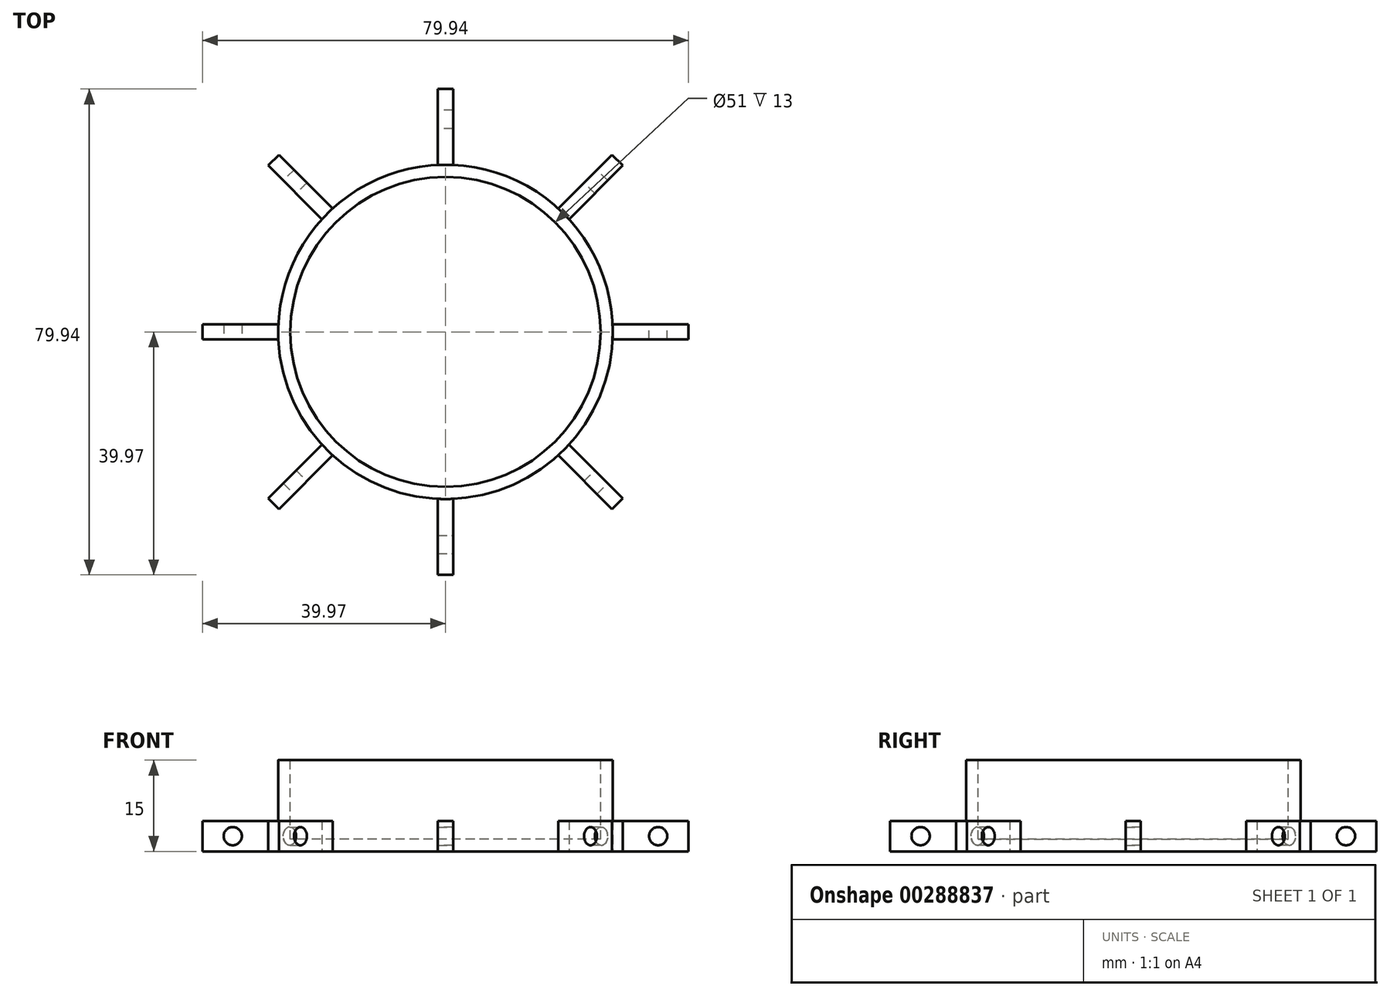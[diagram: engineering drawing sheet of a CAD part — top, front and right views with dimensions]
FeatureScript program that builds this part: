
annotation { "Feature Type Name" : "Feature", "Feature Type Description" : "" }
export const myFeature = defineFeature(function(context is Context, id is Id, definition is map)
    precondition{}
    {
        {
            var Q0;
            Q0=qCreatedBy(makeId("Top.planeOp"),FACE);
            var sketch = newSketch(context, id + "F0", { "sketchPlane" : qUnion([Q0])});
            skCircle(sketch, "E0", {"center": v(0, 0) * mm, "radius": 27.5 * mm});
            skPoint(sketch, "E1", {"position": v(0, 27.5) * mm});
            skLineSegment(sketch, "E2.bottom", {"start": v(1.25, 39.97) * mm, "end": v(-1.25, 39.97) * mm});
            skLineSegment(sketch, "E2.left", {"start": v(1.25, 39.97) * mm, "end": v(1.25, 27.47) * mm});
            skLineSegment(sketch, "E2.right", {"start": v(-1.25, 39.97) * mm, "end": v(-1.25, 27.47) * mm});
            skLineSegment(sketch, "E3.MirrorCS", {"start": v(-1.25, -39.97) * mm, "end": v(-1.25, -27.47) * mm});
            skLineSegment(sketch, "E4.MirrorCS", {"start": v(1.25, -39.97) * mm, "end": v(1.25, -27.47) * mm});
            skLineSegment(sketch, "E5.MirrorCS", {"start": v(1.25, -39.97) * mm, "end": v(-1.25, -39.97) * mm});
            skPoint(sketch, "E6", {"position": v(-27.5, 0) * mm});
            skLineSegment(sketch, "E7.MirrorCS", {"start": v(-39.97, 1.25) * mm, "end": v(-27.47, 1.25) * mm});
            skLineSegment(sketch, "E8.MirrorCS", {"start": v(-39.97, -1.25) * mm, "end": v(-27.47, -1.25) * mm});
            skLineSegment(sketch, "E9.MirrorCS", {"start": v(-39.97, -1.25) * mm, "end": v(-39.97, 1.25) * mm});
            skLineSegment(sketch, "E10.MirrorCS", {"start": v(-27.38, 29.15) * mm, "end": v(-18.54, 20.3) * mm});
            skLineSegment(sketch, "E11.MirrorCS", {"start": v(-29.15, 27.38) * mm, "end": v(-20.3, 18.54) * mm});
            skLineSegment(sketch, "E12.MirrorCS", {"start": v(-29.15, 27.38) * mm, "end": v(-27.38, 29.15) * mm});
            skLineSegment(sketch, "E13.MirrorCS", {"start": v(-27.38, -29.15) * mm, "end": v(-18.54, -20.3) * mm});
            skLineSegment(sketch, "E14.MirrorCS", {"start": v(-29.15, -27.38) * mm, "end": v(-20.3, -18.54) * mm});
            skLineSegment(sketch, "E15.MirrorCS", {"start": v(-29.15, -27.38) * mm, "end": v(-27.38, -29.15) * mm});
            skLineSegment(sketch, "E16.MirrorCS", {"start": v(39.97, 1.25) * mm, "end": v(27.47, 1.25) * mm});
            skLineSegment(sketch, "E17.MirrorCS", {"start": v(39.97, -1.25) * mm, "end": v(27.47, -1.25) * mm});
            skLineSegment(sketch, "E18.MirrorCS", {"start": v(39.97, -1.25) * mm, "end": v(39.97, 1.25) * mm});
            skLineSegment(sketch, "E19.MirrorCS", {"start": v(27.38, -29.15) * mm, "end": v(18.54, -20.3) * mm});
            skLineSegment(sketch, "E20.MirrorCS", {"start": v(29.15, -27.38) * mm, "end": v(20.3, -18.54) * mm});
            skLineSegment(sketch, "E21.MirrorCS", {"start": v(29.15, -27.38) * mm, "end": v(27.38, -29.15) * mm});
            skLineSegment(sketch, "E22.MirrorCS", {"start": v(29.15, 27.38) * mm, "end": v(20.3, 18.54) * mm});
            skLineSegment(sketch, "E23.MirrorCS", {"start": v(27.38, 29.15) * mm, "end": v(18.54, 20.3) * mm});
            skLineSegment(sketch, "E24.MirrorCS", {"start": v(29.15, 27.38) * mm, "end": v(27.38, 29.15) * mm});
            skSolve(sketch);
        }
        {
            var Q0;
            Q0=makeQuery(id+"F0.imprint","IMPRINT",FACE,{"disambiguationData":[TD([[makeQuery(id+"F0.imprint","IMPRINT",EDGE,{"derivedFrom":sQuery(id+"F0.wireOp",EDGE,"E0")}),1.0]])]});
            extrude(context, id + "F1", {"entities" : qUnion([Q0]), "depth" : 15 * mm});
        }
        {
            var Q0;
            Q0=makeQuery(id+"F1.opExtrude","CAP_FACE",FACE,{"disambiguationData":[OSD([sQuery(id+"F0.wireOp",EDGE,"E0")])],"isStart":false});
            var sketch = newSketch(context, id + "F2", { "sketchPlane" : qUnion([Q0])});
            skCircle(sketch, "E25", {"center": v(0, 0) * mm, "radius": 25.5 * mm});
            skSolve(sketch);
        }
        {
            var Q0;
            Q0=makeQuery(id+"F2.imprint","IMPRINT",FACE,{"disambiguationData":[TD([[makeQuery(id+"F2.imprint","IMPRINT",EDGE,{"derivedFrom":sQuery(id+"F2.wireOp",EDGE,"E25")}),1.0]])]});
            extrude(context, id + "F3", {"entities" : qUnion([Q0]), "operationType" : NewBodyOperationType.REMOVE, "oppositeDirection" : true, "depth" : 13 * mm});
        }
        {
            var Q0;
            Q0=makeQuery(id+"F0.imprint","IMPRINT",FACE,{"disambiguationData":[TD([[makeQuery(id+"F0.imprint","IMPRINT",EDGE,{"derivedFrom":sQuery(id+"F0.wireOp",EDGE,"E2.bottom")}),1.0]])]});
            var Q1;
            {var subQ0=sQuery(id+"F0.wireOp",EDGE,"E10.MirrorCS");Q1=makeQuery(id+"F0.imprint","IMPRINT",FACE,{"disambiguationData":[TD([[makeQuery(id+"F0.imprint","IMPRINT",EDGE,{"derivedFrom":subQ0}),-1.0]])]});}
            var Q2;
            {var subQ0=sQuery(id+"F0.wireOp",EDGE,"E7.MirrorCS");Q2=makeQuery(id+"F0.imprint","IMPRINT",FACE,{"disambiguationData":[TD([[makeQuery(id+"F0.imprint","IMPRINT",EDGE,{"derivedFrom":subQ0}),-1.0]])]});}
            var Q3;
            {var subQ0=sQuery(id+"F0.wireOp",EDGE,"E13.MirrorCS");Q3=makeQuery(id+"F0.imprint","IMPRINT",FACE,{"disambiguationData":[TD([[makeQuery(id+"F0.imprint","IMPRINT",EDGE,{"derivedFrom":subQ0}),1.0]])]});}
            var Q4;
            {var subQ0=sQuery(id+"F0.wireOp",EDGE,"E3.MirrorCS");Q4=makeQuery(id+"F0.imprint","IMPRINT",FACE,{"disambiguationData":[TD([[makeQuery(id+"F0.imprint","IMPRINT",EDGE,{"derivedFrom":subQ0}),-1.0]])]});}
            var Q5;
            {var subQ0=sQuery(id+"F0.wireOp",EDGE,"E19.MirrorCS");Q5=makeQuery(id+"F0.imprint","IMPRINT",FACE,{"disambiguationData":[TD([[makeQuery(id+"F0.imprint","IMPRINT",EDGE,{"derivedFrom":subQ0}),-1.0]])]});}
            var Q6;
            {var subQ0=sQuery(id+"F0.wireOp",EDGE,"E16.MirrorCS");Q6=makeQuery(id+"F0.imprint","IMPRINT",FACE,{"disambiguationData":[TD([[makeQuery(id+"F0.imprint","IMPRINT",EDGE,{"derivedFrom":subQ0}),1.0]])]});}
            var Q7;
            {var subQ0=sQuery(id+"F0.wireOp",EDGE,"E22.MirrorCS");Q7=makeQuery(id+"F0.imprint","IMPRINT",FACE,{"disambiguationData":[TD([[makeQuery(id+"F0.imprint","IMPRINT",EDGE,{"derivedFrom":subQ0}),-1.0]])]});}
            extrude(context, id + "F4", {"entities" : qUnion([Q0, Q1, Q2, Q3, Q4, Q5, Q6, Q7]), "operationType" : NewBodyOperationType.ADD, "depth" : 5 * mm});
        }
        {
            var Q0;
            Q0=makeQuery(id+"F4.opExtrude","SWEPT_FACE",FACE,{"disambiguationData":[OSD([sQuery(id+"F0.wireOp",EDGE,"E4.MirrorCS")])]});
            var sketch = newSketch(context, id + "F5", { "sketchPlane" : qUnion([Q0])});
            skLineSegment(sketch, "E26", {"start": v(-39.97, 2.5) * mm, "end": v(-34.97, 2.5) * mm});
            skCircle(sketch, "E27", {"center": v(-34.97, 2.5) * mm, "radius": 1.5 * mm});
            skSolve(sketch);
        }
        {
            var Q0;
            Q0=makeQuery(id+"F5.imprint","IMPRINT",FACE,{"disambiguationData":[TD([[makeQuery(id+"F5.imprint","IMPRINT",EDGE,{"derivedFrom":sQuery(id+"F5.wireOp",EDGE,"E27")}),1.0]])]});
            extrude(context, id + "F6", {"entities" : qUnion([Q0]), "operationType" : NewBodyOperationType.REMOVE, "oppositeDirection" : true, "depth" : 25 * mm});
        }
        {
            var Q0;
            Q0=makeQuery(id+"F4.opExtrude","SWEPT_FACE",FACE,{"disambiguationData":[OSD([sQuery(id+"F0.wireOp",EDGE,"E13.MirrorCS")])]});
            var sketch = newSketch(context, id + "F7", { "sketchPlane" : qUnion([Q0])});
            skLineSegment(sketch, "E28", {"start": v(-39.97, 2.5) * mm, "end": v(-34.97, 2.5) * mm});
            skCircle(sketch, "E29", {"center": v(-34.97, 2.5) * mm, "radius": 1.5 * mm});
            skSolve(sketch);
        }
        {
            var Q0;
            Q0=makeQuery(id+"F7.imprint","IMPRINT",FACE,{"disambiguationData":[TD([[makeQuery(id+"F7.imprint","IMPRINT",EDGE,{"derivedFrom":sQuery(id+"F7.wireOp",EDGE,"E29")}),1.0]])]});
            var Q1;
            Q1=sQuery(id+"F7.wireOp",EDGE,"E29");
            extrude(context, id + "F8", {"entities" : qUnion([Q0]), "operationType" : NewBodyOperationType.REMOVE, "surfaceEntities" : qUnion([Q1]), "oppositeDirection" : true, "depth" : 25 * mm});
        }
        {
            var Q0;
            Q0=makeQuery(id+"F4.opExtrude","SWEPT_FACE",FACE,{"disambiguationData":[OSD([sQuery(id+"F0.wireOp",EDGE,"E8.MirrorCS")])]});
            var sketch = newSketch(context, id + "F9", { "sketchPlane" : qUnion([Q0])});
            skLineSegment(sketch, "E30", {"start": v(-39.97, 2.5) * mm, "end": v(-34.97, 2.5) * mm});
            skPoint(sketch, "E30.endSnap0", {"position": v(-39.97, 2.5) * mm});
            skCircle(sketch, "E31", {"center": v(-34.97, 2.5) * mm, "radius": 1.5 * mm});
            skSolve(sketch);
        }
        {
            var Q0;
            Q0=makeQuery(id+"F9.imprint","IMPRINT",FACE,{"disambiguationData":[TD([[makeQuery(id+"F9.imprint","IMPRINT",EDGE,{"derivedFrom":sQuery(id+"F9.wireOp",EDGE,"E31")}),1.0]])]});
            extrude(context, id + "F10", {"entities" : qUnion([Q0]), "operationType" : NewBodyOperationType.REMOVE, "oppositeDirection" : true, "depth" : 25 * mm});
        }
        {
            var Q0;
            Q0=makeQuery(id+"F4.opExtrude","SWEPT_FACE",FACE,{"disambiguationData":[OSD([sQuery(id+"F0.wireOp",EDGE,"E11.MirrorCS")])]});
            var sketch = newSketch(context, id + "F11", { "sketchPlane" : qUnion([Q0])});
            skLineSegment(sketch, "E32", {"start": v(-39.97, 2.5) * mm, "end": v(-34.97, 2.5) * mm});
            skCircle(sketch, "E33", {"center": v(-34.97, 2.5) * mm, "radius": 1.5 * mm});
            skSolve(sketch);
        }
        {
            var Q0;
            Q0=makeQuery(id+"F11.imprint","IMPRINT",FACE,{"disambiguationData":[TD([[makeQuery(id+"F11.imprint","IMPRINT",EDGE,{"derivedFrom":sQuery(id+"F11.wireOp",EDGE,"E33")}),1.0]])]});
            extrude(context, id + "F12", {"entities" : qUnion([Q0]), "operationType" : NewBodyOperationType.REMOVE, "oppositeDirection" : true, "depth" : 25 * mm});
        }
        {
            var Q0;
            Q0=makeQuery(id+"F4.opExtrude","SWEPT_FACE",FACE,{"disambiguationData":[OSD([sQuery(id+"F0.wireOp",EDGE,"E2.right")])]});
            var sketch = newSketch(context, id + "F13", { "sketchPlane" : qUnion([Q0])});
            skLineSegment(sketch, "E34", {"start": v(-39.97, 2.5) * mm, "end": v(-34.97, 2.5) * mm});
            skCircle(sketch, "E35", {"center": v(-34.97, 2.5) * mm, "radius": 1.5 * mm});
            skSolve(sketch);
        }
        {
            var Q0;
            Q0=makeQuery(id+"F13.imprint","IMPRINT",FACE,{"disambiguationData":[TD([[makeQuery(id+"F13.imprint","IMPRINT",EDGE,{"derivedFrom":sQuery(id+"F13.wireOp",EDGE,"E35")}),1.0]])]});
            extrude(context, id + "F14", {"entities" : qUnion([Q0]), "operationType" : NewBodyOperationType.REMOVE, "oppositeDirection" : true, "depth" : 25 * mm});
        }
        {
            var Q0;
            Q0=makeQuery(id+"F4.opExtrude","SWEPT_FACE",FACE,{"disambiguationData":[OSD([sQuery(id+"F0.wireOp",EDGE,"E23.MirrorCS")])]});
            var sketch = newSketch(context, id + "F15", { "sketchPlane" : qUnion([Q0])});
            skLineSegment(sketch, "E36", {"start": v(-39.97, 2.5) * mm, "end": v(-34.97, 2.5) * mm});
            skCircle(sketch, "E37", {"center": v(-34.97, 2.5) * mm, "radius": 1.5 * mm});
            skSolve(sketch);
        }
        {
            var Q0;
            Q0=makeQuery(id+"F15.imprint","IMPRINT",FACE,{"disambiguationData":[TD([[makeQuery(id+"F15.imprint","IMPRINT",EDGE,{"derivedFrom":sQuery(id+"F15.wireOp",EDGE,"E37")}),1.0]])]});
            extrude(context, id + "F16", {"entities" : qUnion([Q0]), "operationType" : NewBodyOperationType.REMOVE, "oppositeDirection" : true, "depth" : 25 * mm});
        }
        {
            var Q0;
            Q0=makeQuery(id+"F4.opExtrude","SWEPT_FACE",FACE,{"disambiguationData":[OSD([sQuery(id+"F0.wireOp",EDGE,"E16.MirrorCS")])]});
            var sketch = newSketch(context, id + "F17", { "sketchPlane" : qUnion([Q0])});
            skLineSegment(sketch, "E38", {"start": v(-39.97, 2.5) * mm, "end": v(-34.97, 2.5) * mm});
            skCircle(sketch, "E39", {"center": v(-34.97, 2.5) * mm, "radius": 1.5 * mm});
            skSolve(sketch);
        }
        {
            var Q0;
            Q0=makeQuery(id+"F17.imprint","IMPRINT",FACE,{"disambiguationData":[TD([[makeQuery(id+"F17.imprint","IMPRINT",EDGE,{"derivedFrom":sQuery(id+"F17.wireOp",EDGE,"E39")}),1.0]])]});
            extrude(context, id + "F18", {"entities" : qUnion([Q0]), "operationType" : NewBodyOperationType.REMOVE, "oppositeDirection" : true, "depth" : 25 * mm});
        }
        {
            var Q0;
            Q0=makeQuery(id+"F4.opExtrude","SWEPT_FACE",FACE,{"disambiguationData":[OSD([sQuery(id+"F0.wireOp",EDGE,"E20.MirrorCS")])]});
            var sketch = newSketch(context, id + "F19", { "sketchPlane" : qUnion([Q0])});
            skLineSegment(sketch, "E40", {"start": v(-39.97, 2.5) * mm, "end": v(-34.97, 2.5) * mm});
            skCircle(sketch, "E41", {"center": v(-34.97, 2.5) * mm, "radius": 1.5 * mm});
            skSolve(sketch);
        }
        {
            var Q0;
            Q0=makeQuery(id+"F19.imprint","IMPRINT",FACE,{"disambiguationData":[TD([[makeQuery(id+"F19.imprint","IMPRINT",EDGE,{"derivedFrom":sQuery(id+"F19.wireOp",EDGE,"E41")}),1.0]])]});
            extrude(context, id + "F20", {"entities" : qUnion([Q0]), "operationType" : NewBodyOperationType.REMOVE, "oppositeDirection" : true, "depth" : 25 * mm});
        }
    });
